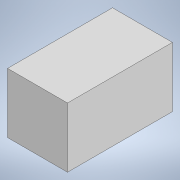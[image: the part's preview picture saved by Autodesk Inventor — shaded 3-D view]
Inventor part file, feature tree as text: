
AUTODESK INVENTOR PART (.ipt)
format: ipt  version: 2022.1 (Build 261234000, 234)  size: 88,576 bytes
history: native  units: in
note: dims shown in document units (in); Inventor stores cm internally (conversion verified against a paired STEP export)
features: extrude x1, sketch x1
ambient origin geometry x8: Origin, YZ Plane, XZ Plane, XY Plane, X Axis, Y Axis, Z Axis, Center Point
bodies: Solid1 (feature_tree)
feature tree (2):
  extrude  "Extrusion1"  Depth=2.0in
  sketch  "Sketch1"  dims[d0=2.0in d1=2.0in d2=3.5in d3=0.0in]
